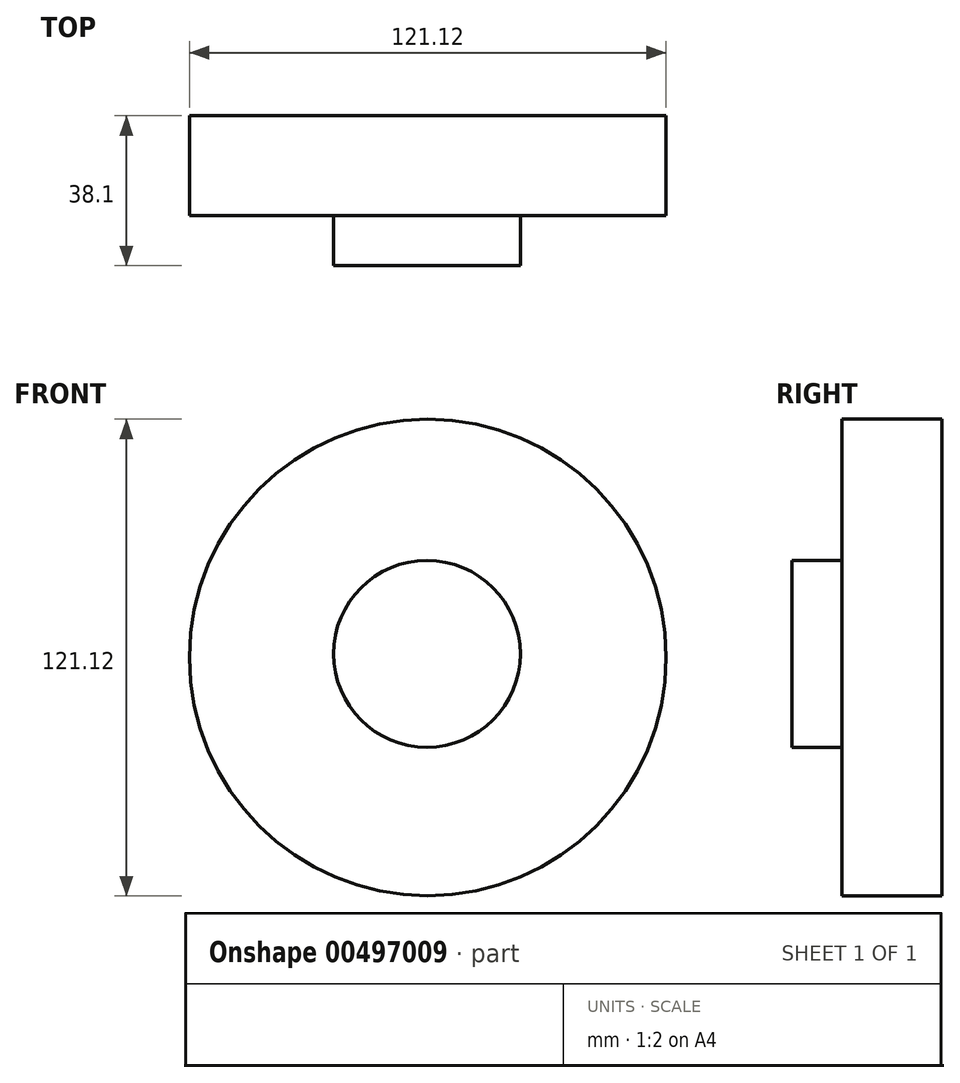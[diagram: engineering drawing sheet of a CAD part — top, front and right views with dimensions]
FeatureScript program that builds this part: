
annotation { "Feature Type Name" : "Feature", "Feature Type Description" : "" }
export const myFeature = defineFeature(function(context is Context, id is Id, definition is map)
    precondition{}
    {
        {
            var Q0;
            Q0=qCreatedBy(makeId("Front.planeOp"),FACE);
            var sketch = newSketch(context, id + "F0", { "sketchPlane" : qUnion([Q0])});
            skCircle(sketch, "E0", {"center": v(0, 0) * mm, "radius": 60.56 * mm});
            skSolve(sketch);
        }
        {
            var Q0;
            Q0=makeQuery(id+"F0.imprint","IMPRINT",FACE,{"disambiguationData":[TD([[makeQuery(id+"F0.imprint","IMPRINT",EDGE,{"derivedFrom":sQuery(id+"F0.wireOp",EDGE,"E0")}),1.0]])]});
            extrude(context, id + "F1", {"entities" : qUnion([Q0]), "depth" : 25.4 * mm});
        }
        {
            var Q0;
            Q0=qCreatedBy(makeId("Front.planeOp"),FACE);
            var sketch = newSketch(context, id + "F2", { "sketchPlane" : qUnion([Q0])});
            skCircle(sketch, "E1", {"center": v(-0.21, 0.93) * mm, "radius": 23.72 * mm});
            skPoint(sketch, "E1.first.point", {"position": v(0, -22.8) * mm});
            skPoint(sketch, "E1.second.point", {"position": v(0, 24.65) * mm});
            skPoint(sketch, "E1.third.point", {"position": v(19.3, -12.56) * mm});
            skSolve(sketch);
        }
        {
            var Q0;
            Q0=qSketchRegion(id+"F2",true);
            extrude(context, id + "F3", {"entities" : qUnion([Q0]), "operationType" : NewBodyOperationType.ADD, "depth" : 38.1 * mm});
        }
    });
